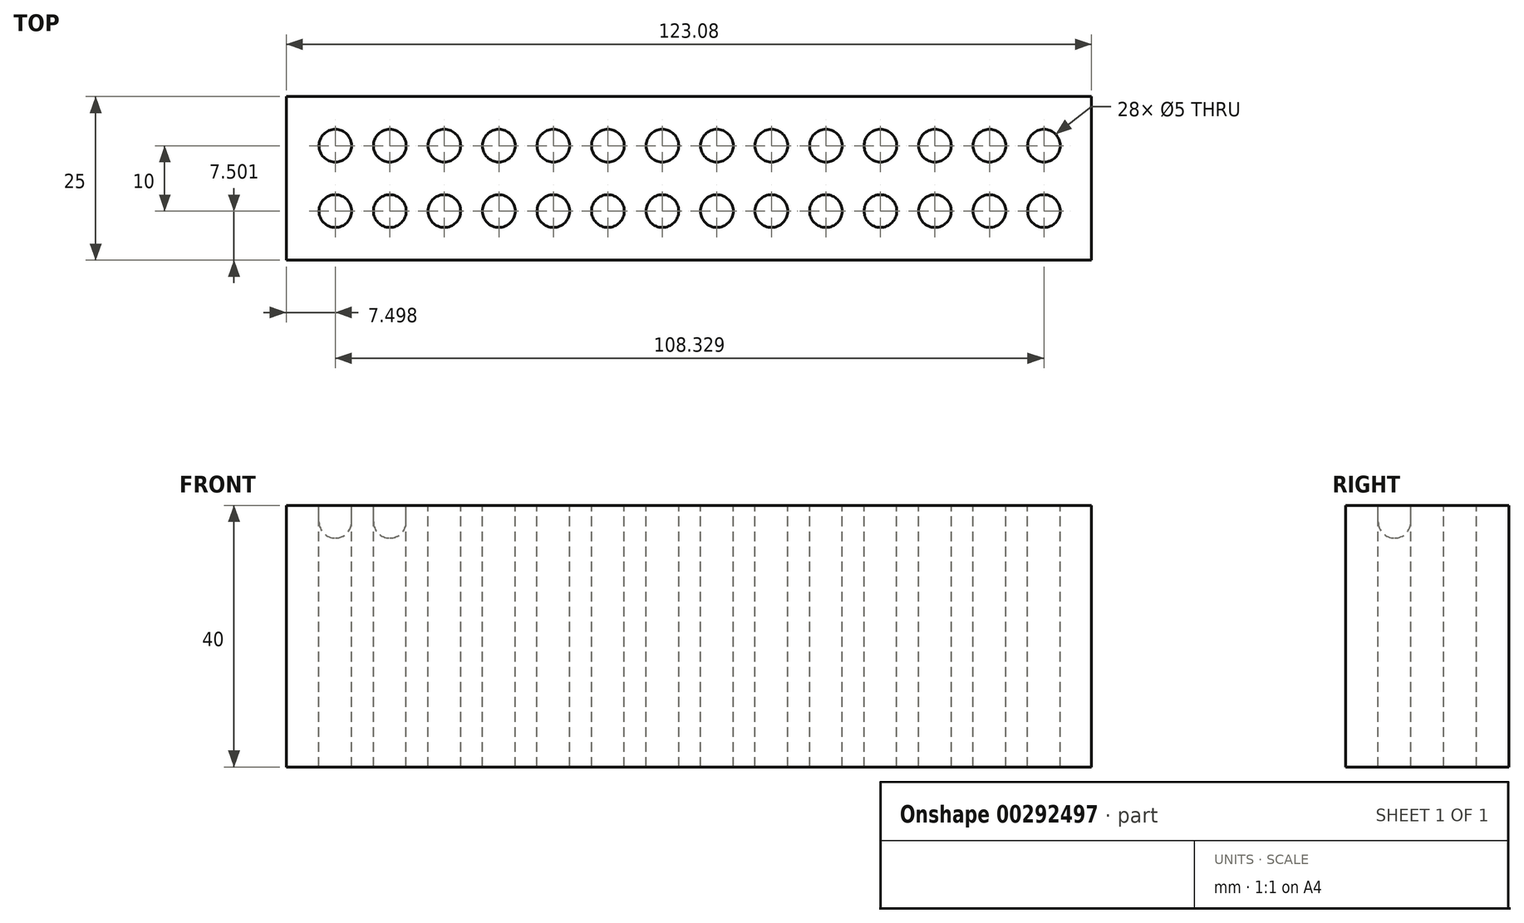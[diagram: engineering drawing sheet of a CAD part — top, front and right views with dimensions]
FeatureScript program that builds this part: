
annotation { "Feature Type Name" : "Feature", "Feature Type Description" : "" }
export const myFeature = defineFeature(function(context is Context, id is Id, definition is map)
    precondition{}
    {
        {
            var Q0;
            Q0=qCreatedBy(makeId("Top.planeOp"),FACE);
            var sketch = newSketch(context, id + "F0", { "sketchPlane" : qUnion([Q0])});
            skLineSegment(sketch, "E0.bottom", {"start": v(-42.9, 15.92) * mm, "end": v(80.2, 15.92) * mm});
            skLineSegment(sketch, "E0.top", {"start": v(-42.9, -9.08) * mm, "end": v(80.2, -9.08) * mm});
            skLineSegment(sketch, "E0.left", {"start": v(-42.9, 15.92) * mm, "end": v(-42.9, -9.08) * mm});
            skLineSegment(sketch, "E0.right", {"start": v(80.2, 15.92) * mm, "end": v(80.2, -9.08) * mm});
            skCircle(sketch, "E1", {"center": v(-35.4, 8.42) * mm, "radius": 2.5 * mm});
            skCircle(sketch, "E2.1.0.0", {"center": v(-27.06, 8.42) * mm, "radius": 2.5 * mm});
            skLineSegment(sketch, "E2.direction1", {"start": v(-35.4, 8.42) * mm, "end": v(-27.06, 8.42) * mm, "construction": true});
            skCircle(sketch, "E3", {"center": v(-35.4, -1.58) * mm, "radius": 2.5 * mm});
            skCircle(sketch, "E4.1.0.0", {"center": v(-27.06, -1.58) * mm, "radius": 2.5 * mm});
            skLineSegment(sketch, "E4.direction1", {"start": v(-35.4, -1.58) * mm, "end": v(-27.06, -1.58) * mm, "construction": true});
            skCircle(sketch, "E5.0.2.0", {"center": v(-18.73, 8.42) * mm, "radius": 2.5 * mm});
            skCircle(sketch, "E5.0.3.0", {"center": v(-10.4, 8.42) * mm, "radius": 2.5 * mm});
            skCircle(sketch, "E5.0.4.0", {"center": v(-2.06, 8.42) * mm, "radius": 2.5 * mm});
            skCircle(sketch, "E5.0.5.0", {"center": v(6.27, 8.42) * mm, "radius": 2.5 * mm});
            skCircle(sketch, "E5.0.6.0", {"center": v(14.6, 8.42) * mm, "radius": 2.5 * mm});
            skCircle(sketch, "E5.0.7.0", {"center": v(22.94, 8.42) * mm, "radius": 2.5 * mm});
            skCircle(sketch, "E5.0.8.0", {"center": v(31.27, 8.42) * mm, "radius": 2.5 * mm});
            skCircle(sketch, "E5.0.9.0", {"center": v(39.6, 8.42) * mm, "radius": 2.5 * mm});
            skCircle(sketch, "E5.0.10.0", {"center": v(47.94, 8.42) * mm, "radius": 2.5 * mm});
            skCircle(sketch, "E5.0.11.0", {"center": v(56.27, 8.42) * mm, "radius": 2.5 * mm});
            skCircle(sketch, "E5.0.12.0", {"center": v(64.6, 8.42) * mm, "radius": 2.5 * mm});
            skCircle(sketch, "E5.0.13.0", {"center": v(72.94, 8.42) * mm, "radius": 2.5 * mm});
            skCircle(sketch, "E6.0.2.0", {"center": v(-18.73, -1.58) * mm, "radius": 2.5 * mm});
            skCircle(sketch, "E6.0.3.0", {"center": v(-10.4, -1.58) * mm, "radius": 2.5 * mm});
            skCircle(sketch, "E6.0.4.0", {"center": v(-2.06, -1.58) * mm, "radius": 2.5 * mm});
            skCircle(sketch, "E6.0.5.0", {"center": v(6.27, -1.58) * mm, "radius": 2.5 * mm});
            skCircle(sketch, "E6.0.6.0", {"center": v(14.6, -1.58) * mm, "radius": 2.5 * mm});
            skCircle(sketch, "E6.0.7.0", {"center": v(22.94, -1.58) * mm, "radius": 2.5 * mm});
            skCircle(sketch, "E6.0.8.0", {"center": v(31.27, -1.58) * mm, "radius": 2.5 * mm});
            skCircle(sketch, "E6.0.9.0", {"center": v(39.6, -1.58) * mm, "radius": 2.5 * mm});
            skCircle(sketch, "E6.0.10.0", {"center": v(47.94, -1.58) * mm, "radius": 2.5 * mm});
            skCircle(sketch, "E6.0.11.0", {"center": v(56.27, -1.58) * mm, "radius": 2.5 * mm});
            skCircle(sketch, "E6.0.12.0", {"center": v(64.6, -1.58) * mm, "radius": 2.5 * mm});
            skCircle(sketch, "E6.0.13.0", {"center": v(72.94, -1.58) * mm, "radius": 2.5 * mm});
            skSolve(sketch);
        }
        {
            var Q0;
            Q0=makeQuery(id+"F0.imprint","IMPRINT",FACE,{"disambiguationData":[TD([[makeQuery(id+"F0.imprint","IMPRINT",EDGE,{"derivedFrom":sQuery(id+"F0.wireOp",EDGE,"E0.bottom")}),-1.0]])]});
            var Q1;
            Q1=makeQuery(id+"F0.imprint","IMPRINT",FACE,{"disambiguationData":[TD([[makeQuery(id+"F0.imprint","IMPRINT",EDGE,{"derivedFrom":sQuery(id+"F0.wireOp",EDGE,"E1")}),1.0]])]});
            var Q2;
            Q2=makeQuery(id+"F0.imprint","IMPRINT",FACE,{"disambiguationData":[TD([[makeQuery(id+"F0.imprint","IMPRINT",EDGE,{"derivedFrom":sQuery(id+"F0.wireOp",EDGE,"E2.1.0.0")}),1.0]])]});
            var Q3;
            Q3=makeQuery(id+"F0.imprint","IMPRINT",FACE,{"disambiguationData":[TD([[makeQuery(id+"F0.imprint","IMPRINT",EDGE,{"derivedFrom":sQuery(id+"F0.wireOp",EDGE,"E2.2.0.0")}),1.0]])]});
            var Q4;
            Q4=makeQuery(id+"F0.imprint","IMPRINT",FACE,{"disambiguationData":[TD([[makeQuery(id+"F0.imprint","IMPRINT",EDGE,{"derivedFrom":sQuery(id+"F0.wireOp",EDGE,"E2.3.0.0")}),1.0]])]});
            var Q5;
            Q5=makeQuery(id+"F0.imprint","IMPRINT",FACE,{"disambiguationData":[TD([[makeQuery(id+"F0.imprint","IMPRINT",EDGE,{"derivedFrom":sQuery(id+"F0.wireOp",EDGE,"E2.4.0.0")}),1.0]])]});
            var Q6;
            Q6=makeQuery(id+"F0.imprint","IMPRINT",FACE,{"disambiguationData":[TD([[makeQuery(id+"F0.imprint","IMPRINT",EDGE,{"derivedFrom":sQuery(id+"F0.wireOp",EDGE,"E2.5.0.0")}),1.0]])]});
            var Q7;
            Q7=makeQuery(id+"F0.imprint","IMPRINT",FACE,{"disambiguationData":[TD([[makeQuery(id+"F0.imprint","IMPRINT",EDGE,{"derivedFrom":sQuery(id+"F0.wireOp",EDGE,"E2.6.0.0")}),1.0]])]});
            var Q8;
            Q8=makeQuery(id+"F0.imprint","IMPRINT",FACE,{"disambiguationData":[TD([[makeQuery(id+"F0.imprint","IMPRINT",EDGE,{"derivedFrom":sQuery(id+"F0.wireOp",EDGE,"E2.7.0.0")}),1.0]])]});
            var Q9;
            Q9=makeQuery(id+"F0.imprint","IMPRINT",FACE,{"disambiguationData":[TD([[makeQuery(id+"F0.imprint","IMPRINT",EDGE,{"derivedFrom":sQuery(id+"F0.wireOp",EDGE,"E2.8.0.0")}),1.0]])]});
            var Q10;
            Q10=makeQuery(id+"F0.imprint","IMPRINT",FACE,{"disambiguationData":[TD([[makeQuery(id+"F0.imprint","IMPRINT",EDGE,{"derivedFrom":sQuery(id+"F0.wireOp",EDGE,"E2.9.0.0")}),1.0]])]});
            var Q11;
            Q11=makeQuery(id+"F0.imprint","IMPRINT",FACE,{"disambiguationData":[TD([[makeQuery(id+"F0.imprint","IMPRINT",EDGE,{"derivedFrom":sQuery(id+"F0.wireOp",EDGE,"E2.10.0.0")}),1.0]])]});
            var Q12;
            Q12=makeQuery(id+"F0.imprint","IMPRINT",FACE,{"disambiguationData":[TD([[makeQuery(id+"F0.imprint","IMPRINT",EDGE,{"derivedFrom":sQuery(id+"F0.wireOp",EDGE,"E2.11.0.0")}),1.0]])]});
            var Q13;
            Q13=makeQuery(id+"F0.imprint","IMPRINT",FACE,{"disambiguationData":[TD([[makeQuery(id+"F0.imprint","IMPRINT",EDGE,{"derivedFrom":sQuery(id+"F0.wireOp",EDGE,"E2.12.0.0")}),1.0]])]});
            var Q14;
            Q14=makeQuery(id+"F0.imprint","IMPRINT",FACE,{"disambiguationData":[TD([[makeQuery(id+"F0.imprint","IMPRINT",EDGE,{"derivedFrom":sQuery(id+"F0.wireOp",EDGE,"E2.13.0.0")}),1.0]])]});
            var Q15;
            Q15=makeQuery(id+"F0.imprint","IMPRINT",FACE,{"disambiguationData":[TD([[makeQuery(id+"F0.imprint","IMPRINT",EDGE,{"derivedFrom":sQuery(id+"F0.wireOp",EDGE,"E2.14.0.0")}),1.0]])]});
            var Q16;
            Q16=makeQuery(id+"F0.imprint","IMPRINT",FACE,{"disambiguationData":[TD([[makeQuery(id+"F0.imprint","IMPRINT",EDGE,{"derivedFrom":sQuery(id+"F0.wireOp",EDGE,"E4.14.0.0")}),1.0]])]});
            var Q17;
            Q17=makeQuery(id+"F0.imprint","IMPRINT",FACE,{"disambiguationData":[TD([[makeQuery(id+"F0.imprint","IMPRINT",EDGE,{"derivedFrom":sQuery(id+"F0.wireOp",EDGE,"E4.13.0.0")}),1.0]])]});
            var Q18;
            Q18=makeQuery(id+"F0.imprint","IMPRINT",FACE,{"disambiguationData":[TD([[makeQuery(id+"F0.imprint","IMPRINT",EDGE,{"derivedFrom":sQuery(id+"F0.wireOp",EDGE,"E4.12.0.0")}),1.0]])]});
            var Q19;
            Q19=makeQuery(id+"F0.imprint","IMPRINT",FACE,{"disambiguationData":[TD([[makeQuery(id+"F0.imprint","IMPRINT",EDGE,{"derivedFrom":sQuery(id+"F0.wireOp",EDGE,"E4.11.0.0")}),1.0]])]});
            var Q20;
            Q20=makeQuery(id+"F0.imprint","IMPRINT",FACE,{"disambiguationData":[TD([[makeQuery(id+"F0.imprint","IMPRINT",EDGE,{"derivedFrom":sQuery(id+"F0.wireOp",EDGE,"E4.10.0.0")}),1.0]])]});
            var Q21;
            Q21=makeQuery(id+"F0.imprint","IMPRINT",FACE,{"disambiguationData":[TD([[makeQuery(id+"F0.imprint","IMPRINT",EDGE,{"derivedFrom":sQuery(id+"F0.wireOp",EDGE,"E4.9.0.0")}),1.0]])]});
            var Q22;
            Q22=makeQuery(id+"F0.imprint","IMPRINT",FACE,{"disambiguationData":[TD([[makeQuery(id+"F0.imprint","IMPRINT",EDGE,{"derivedFrom":sQuery(id+"F0.wireOp",EDGE,"E4.8.0.0")}),1.0]])]});
            var Q23;
            Q23=makeQuery(id+"F0.imprint","IMPRINT",FACE,{"disambiguationData":[TD([[makeQuery(id+"F0.imprint","IMPRINT",EDGE,{"derivedFrom":sQuery(id+"F0.wireOp",EDGE,"E4.7.0.0")}),1.0]])]});
            var Q24;
            Q24=makeQuery(id+"F0.imprint","IMPRINT",FACE,{"disambiguationData":[TD([[makeQuery(id+"F0.imprint","IMPRINT",EDGE,{"derivedFrom":sQuery(id+"F0.wireOp",EDGE,"E4.6.0.0")}),1.0]])]});
            var Q25;
            Q25=makeQuery(id+"F0.imprint","IMPRINT",FACE,{"disambiguationData":[TD([[makeQuery(id+"F0.imprint","IMPRINT",EDGE,{"derivedFrom":sQuery(id+"F0.wireOp",EDGE,"E4.5.0.0")}),1.0]])]});
            var Q26;
            Q26=makeQuery(id+"F0.imprint","IMPRINT",FACE,{"disambiguationData":[TD([[makeQuery(id+"F0.imprint","IMPRINT",EDGE,{"derivedFrom":sQuery(id+"F0.wireOp",EDGE,"E4.4.0.0")}),1.0]])]});
            var Q27;
            Q27=makeQuery(id+"F0.imprint","IMPRINT",FACE,{"disambiguationData":[TD([[makeQuery(id+"F0.imprint","IMPRINT",EDGE,{"derivedFrom":sQuery(id+"F0.wireOp",EDGE,"E4.3.0.0")}),1.0]])]});
            var Q28;
            Q28=makeQuery(id+"F0.imprint","IMPRINT",FACE,{"disambiguationData":[TD([[makeQuery(id+"F0.imprint","IMPRINT",EDGE,{"derivedFrom":sQuery(id+"F0.wireOp",EDGE,"E4.2.0.0")}),1.0]])]});
            var Q29;
            Q29=makeQuery(id+"F0.imprint","IMPRINT",FACE,{"disambiguationData":[TD([[makeQuery(id+"F0.imprint","IMPRINT",EDGE,{"derivedFrom":sQuery(id+"F0.wireOp",EDGE,"E4.1.0.0")}),1.0]])]});
            var Q30;
            Q30=makeQuery(id+"F0.imprint","IMPRINT",FACE,{"disambiguationData":[TD([[makeQuery(id+"F0.imprint","IMPRINT",EDGE,{"derivedFrom":sQuery(id+"F0.wireOp",EDGE,"E3")}),1.0]])]});
            extrude(context, id + "F1", {"entities" : qUnion([Q0, Q1, Q2, Q3, Q4, Q5, Q6, Q7, Q8, Q9, Q10, Q11, Q12, Q13, Q14, Q15, Q16, Q17, Q18, Q19, Q20, Q21, Q22, Q23, Q24, Q25, Q26, Q27, Q28, Q29, Q30]), "oppositeDirection" : true, "depth" : 40 * mm});
        }
        {
            var Q0;
            Q0=makeQuery(id+"F0.imprint","IMPRINT",FACE,{"disambiguationData":[TD([[makeQuery(id+"F0.imprint","IMPRINT",EDGE,{"derivedFrom":sQuery(id+"F0.wireOp",EDGE,"E1")}),1.0]])]});
            var Q1;
            Q1=makeQuery(id+"F0.imprint","IMPRINT",FACE,{"disambiguationData":[TD([[makeQuery(id+"F0.imprint","IMPRINT",EDGE,{"derivedFrom":sQuery(id+"F0.wireOp",EDGE,"E2.1.0.0")}),1.0]])]});
            var Q2;
            Q2=makeQuery(id+"F0.imprint","IMPRINT",FACE,{"disambiguationData":[TD([[makeQuery(id+"F0.imprint","IMPRINT",EDGE,{"derivedFrom":sQuery(id+"F0.wireOp",EDGE,"E5.0.2.0")}),1.0]])]});
            var Q3;
            Q3=makeQuery(id+"F0.imprint","IMPRINT",FACE,{"disambiguationData":[TD([[makeQuery(id+"F0.imprint","IMPRINT",EDGE,{"derivedFrom":sQuery(id+"F0.wireOp",EDGE,"E5.0.3.0")}),1.0]])]});
            var Q4;
            Q4=makeQuery(id+"F0.imprint","IMPRINT",FACE,{"disambiguationData":[TD([[makeQuery(id+"F0.imprint","IMPRINT",EDGE,{"derivedFrom":sQuery(id+"F0.wireOp",EDGE,"E5.0.4.0")}),1.0]])]});
            var Q5;
            Q5=makeQuery(id+"F0.imprint","IMPRINT",FACE,{"disambiguationData":[TD([[makeQuery(id+"F0.imprint","IMPRINT",EDGE,{"derivedFrom":sQuery(id+"F0.wireOp",EDGE,"E5.0.5.0")}),1.0]])]});
            var Q6;
            Q6=makeQuery(id+"F0.imprint","IMPRINT",FACE,{"disambiguationData":[TD([[makeQuery(id+"F0.imprint","IMPRINT",EDGE,{"derivedFrom":sQuery(id+"F0.wireOp",EDGE,"E5.0.6.0")}),1.0]])]});
            var Q7;
            Q7=makeQuery(id+"F0.imprint","IMPRINT",FACE,{"disambiguationData":[TD([[makeQuery(id+"F0.imprint","IMPRINT",EDGE,{"derivedFrom":sQuery(id+"F0.wireOp",EDGE,"E5.0.7.0")}),1.0]])]});
            var Q8;
            Q8=makeQuery(id+"F0.imprint","IMPRINT",FACE,{"disambiguationData":[TD([[makeQuery(id+"F0.imprint","IMPRINT",EDGE,{"derivedFrom":sQuery(id+"F0.wireOp",EDGE,"E5.0.8.0")}),1.0]])]});
            var Q9;
            Q9=makeQuery(id+"F0.imprint","IMPRINT",FACE,{"disambiguationData":[TD([[makeQuery(id+"F0.imprint","IMPRINT",EDGE,{"derivedFrom":sQuery(id+"F0.wireOp",EDGE,"E5.0.9.0")}),1.0]])]});
            var Q10;
            Q10=makeQuery(id+"F0.imprint","IMPRINT",FACE,{"disambiguationData":[TD([[makeQuery(id+"F0.imprint","IMPRINT",EDGE,{"derivedFrom":sQuery(id+"F0.wireOp",EDGE,"E5.0.10.0")}),1.0]])]});
            var Q11;
            Q11=makeQuery(id+"F0.imprint","IMPRINT",FACE,{"disambiguationData":[TD([[makeQuery(id+"F0.imprint","IMPRINT",EDGE,{"derivedFrom":sQuery(id+"F0.wireOp",EDGE,"E5.0.11.0")}),1.0]])]});
            var Q12;
            Q12=makeQuery(id+"F0.imprint","IMPRINT",FACE,{"disambiguationData":[TD([[makeQuery(id+"F0.imprint","IMPRINT",EDGE,{"derivedFrom":sQuery(id+"F0.wireOp",EDGE,"E5.0.12.0")}),1.0]])]});
            var Q13;
            Q13=makeQuery(id+"F0.imprint","IMPRINT",FACE,{"disambiguationData":[TD([[makeQuery(id+"F0.imprint","IMPRINT",EDGE,{"derivedFrom":sQuery(id+"F0.wireOp",EDGE,"E5.0.13.0")}),1.0]])]});
            extrude(context, id + "F2", {"entities" : qUnion([Q0, Q1, Q2, Q3, Q4, Q5, Q6, Q7, Q8, Q9, Q10, Q11, Q12, Q13]), "operationType" : NewBodyOperationType.REMOVE, "oppositeDirection" : true, "depth" : 40 * mm});
        }
        {
            var Q0;
            Q0=makeQuery(id+"F0.imprint","IMPRINT",FACE,{"disambiguationData":[TD([[makeQuery(id+"F0.imprint","IMPRINT",EDGE,{"derivedFrom":sQuery(id+"F0.wireOp",EDGE,"E3")}),1.0]])]});
            var Q1;
            Q1=makeQuery(id+"F0.imprint","IMPRINT",FACE,{"disambiguationData":[TD([[makeQuery(id+"F0.imprint","IMPRINT",EDGE,{"derivedFrom":sQuery(id+"F0.wireOp",EDGE,"E4.1.0.0")}),1.0]])]});
            var Q2;
            Q2=makeQuery(id+"F0.imprint","IMPRINT",FACE,{"disambiguationData":[TD([[makeQuery(id+"F0.imprint","IMPRINT",EDGE,{"derivedFrom":sQuery(id+"F0.wireOp",EDGE,"E4.2.0.0")}),1.0]])]});
            var Q3;
            Q3=makeQuery(id+"F0.imprint","IMPRINT",FACE,{"disambiguationData":[TD([[makeQuery(id+"F0.imprint","IMPRINT",EDGE,{"derivedFrom":sQuery(id+"F0.wireOp",EDGE,"E4.3.0.0")}),1.0]])]});
            var Q4;
            Q4=makeQuery(id+"F0.imprint","IMPRINT",FACE,{"disambiguationData":[TD([[makeQuery(id+"F0.imprint","IMPRINT",EDGE,{"derivedFrom":sQuery(id+"F0.wireOp",EDGE,"E4.4.0.0")}),1.0]])]});
            var Q5;
            Q5=makeQuery(id+"F0.imprint","IMPRINT",FACE,{"disambiguationData":[TD([[makeQuery(id+"F0.imprint","IMPRINT",EDGE,{"derivedFrom":sQuery(id+"F0.wireOp",EDGE,"E4.5.0.0")}),1.0]])]});
            var Q6;
            Q6=makeQuery(id+"F0.imprint","IMPRINT",FACE,{"disambiguationData":[TD([[makeQuery(id+"F0.imprint","IMPRINT",EDGE,{"derivedFrom":sQuery(id+"F0.wireOp",EDGE,"E4.6.0.0")}),1.0]])]});
            var Q7;
            Q7=makeQuery(id+"F0.imprint","IMPRINT",FACE,{"disambiguationData":[TD([[makeQuery(id+"F0.imprint","IMPRINT",EDGE,{"derivedFrom":sQuery(id+"F0.wireOp",EDGE,"E4.7.0.0")}),1.0]])]});
            var Q8;
            Q8=makeQuery(id+"F0.imprint","IMPRINT",FACE,{"disambiguationData":[TD([[makeQuery(id+"F0.imprint","IMPRINT",EDGE,{"derivedFrom":sQuery(id+"F0.wireOp",EDGE,"E4.8.0.0")}),1.0]])]});
            var Q9;
            Q9=makeQuery(id+"F0.imprint","IMPRINT",FACE,{"disambiguationData":[TD([[makeQuery(id+"F0.imprint","IMPRINT",EDGE,{"derivedFrom":sQuery(id+"F0.wireOp",EDGE,"E4.9.0.0")}),1.0]])]});
            var Q10;
            Q10=makeQuery(id+"F0.imprint","IMPRINT",FACE,{"disambiguationData":[TD([[makeQuery(id+"F0.imprint","IMPRINT",EDGE,{"derivedFrom":sQuery(id+"F0.wireOp",EDGE,"E4.10.0.0")}),1.0]])]});
            var Q11;
            Q11=makeQuery(id+"F0.imprint","IMPRINT",FACE,{"disambiguationData":[TD([[makeQuery(id+"F0.imprint","IMPRINT",EDGE,{"derivedFrom":sQuery(id+"F0.wireOp",EDGE,"E4.11.0.0")}),1.0]])]});
            var Q12;
            Q12=makeQuery(id+"F0.imprint","IMPRINT",FACE,{"disambiguationData":[TD([[makeQuery(id+"F0.imprint","IMPRINT",EDGE,{"derivedFrom":sQuery(id+"F0.wireOp",EDGE,"E4.12.0.0")}),1.0]])]});
            var Q13;
            Q13=makeQuery(id+"F0.imprint","IMPRINT",FACE,{"disambiguationData":[TD([[makeQuery(id+"F0.imprint","IMPRINT",EDGE,{"derivedFrom":sQuery(id+"F0.wireOp",EDGE,"E4.13.0.0")}),1.0]])]});
            var Q14;
            Q14=makeQuery(id+"F0.imprint","IMPRINT",FACE,{"disambiguationData":[TD([[makeQuery(id+"F0.imprint","IMPRINT",EDGE,{"derivedFrom":sQuery(id+"F0.wireOp",EDGE,"E4.14.0.0")}),1.0]])]});
            extrude(context, id + "F3", {"entities" : qUnion([Q0, Q1, Q2, Q3, Q4, Q5, Q6, Q7, Q8, Q9, Q10, Q11, Q12, Q13, Q14]), "operationType" : NewBodyOperationType.REMOVE, "oppositeDirection" : true, "depth" : 5 * mm});
        }
        {
            var Q0;
            Q0=makeQuery(id+"F3.boolean.opBoolean","COPY",EDGE,{"derivedFrom":makeQuery(id+"F3.opExtrude","CAP_EDGE",EDGE,{"disambiguationData":[OSD([sQuery(id+"F0.wireOp",EDGE,"E3")])],"isStart":false})});
            var Q1;
            Q1=makeQuery(id+"F3.boolean.opBoolean","COPY",EDGE,{"derivedFrom":makeQuery(id+"F3.opExtrude","CAP_EDGE",EDGE,{"disambiguationData":[OSD([sQuery(id+"F0.wireOp",EDGE,"E4.1.0.0")])],"isStart":false})});
            var Q2;
            Q2=makeQuery(id+"F3.boolean.opBoolean","COPY",EDGE,{"derivedFrom":makeQuery(id+"F3.opExtrude","CAP_EDGE",EDGE,{"disambiguationData":[OSD([sQuery(id+"F0.wireOp",EDGE,"E4.2.0.0")])],"isStart":false})});
            var Q3;
            Q3=makeQuery(id+"F3.boolean.opBoolean","COPY",EDGE,{"derivedFrom":makeQuery(id+"F3.opExtrude","CAP_EDGE",EDGE,{"disambiguationData":[OSD([sQuery(id+"F0.wireOp",EDGE,"E4.3.0.0")])],"isStart":false})});
            var Q4;
            Q4=makeQuery(id+"F3.boolean.opBoolean","COPY",EDGE,{"derivedFrom":makeQuery(id+"F3.opExtrude","CAP_EDGE",EDGE,{"disambiguationData":[OSD([sQuery(id+"F0.wireOp",EDGE,"E4.4.0.0")])],"isStart":false})});
            var Q5;
            Q5=makeQuery(id+"F3.boolean.opBoolean","COPY",EDGE,{"derivedFrom":makeQuery(id+"F3.opExtrude","CAP_EDGE",EDGE,{"disambiguationData":[OSD([sQuery(id+"F0.wireOp",EDGE,"E4.5.0.0")])],"isStart":false})});
            var Q6;
            Q6=makeQuery(id+"F3.boolean.opBoolean","COPY",EDGE,{"derivedFrom":makeQuery(id+"F3.opExtrude","CAP_EDGE",EDGE,{"disambiguationData":[OSD([sQuery(id+"F0.wireOp",EDGE,"E4.6.0.0")])],"isStart":false})});
            var Q7;
            Q7=makeQuery(id+"F3.boolean.opBoolean","COPY",EDGE,{"derivedFrom":makeQuery(id+"F3.opExtrude","CAP_EDGE",EDGE,{"disambiguationData":[OSD([sQuery(id+"F0.wireOp",EDGE,"E4.7.0.0")])],"isStart":false})});
            var Q8;
            Q8=makeQuery(id+"F3.boolean.opBoolean","COPY",FACE,{"derivedFrom":makeQuery(id+"F3.opExtrude","CAP_FACE",FACE,{"disambiguationData":[OSD([sQuery(id+"F0.wireOp",EDGE,"E4.8.0.0")])],"isStart":false})});
            var Q9;
            Q9=makeQuery(id+"F3.boolean.opBoolean","COPY",EDGE,{"derivedFrom":makeQuery(id+"F3.opExtrude","CAP_EDGE",EDGE,{"disambiguationData":[OSD([sQuery(id+"F0.wireOp",EDGE,"E4.9.0.0")])],"isStart":false})});
            var Q10;
            Q10=makeQuery(id+"F3.boolean.opBoolean","COPY",EDGE,{"derivedFrom":makeQuery(id+"F3.opExtrude","CAP_EDGE",EDGE,{"disambiguationData":[OSD([sQuery(id+"F0.wireOp",EDGE,"E4.10.0.0")])],"isStart":false})});
            var Q11;
            Q11=makeQuery(id+"F3.boolean.opBoolean","COPY",FACE,{"derivedFrom":makeQuery(id+"F3.opExtrude","CAP_FACE",FACE,{"disambiguationData":[OSD([sQuery(id+"F0.wireOp",EDGE,"E4.11.0.0")])],"isStart":false})});
            var Q12;
            Q12=makeQuery(id+"F3.boolean.opBoolean","COPY",FACE,{"derivedFrom":makeQuery(id+"F3.opExtrude","CAP_FACE",FACE,{"disambiguationData":[OSD([sQuery(id+"F0.wireOp",EDGE,"E4.12.0.0")])],"isStart":false})});
            var Q13;
            Q13=makeQuery(id+"F3.boolean.opBoolean","COPY",EDGE,{"derivedFrom":makeQuery(id+"F3.opExtrude","CAP_EDGE",EDGE,{"disambiguationData":[OSD([sQuery(id+"F0.wireOp",EDGE,"E4.13.0.0")])],"isStart":false})});
            var Q14;
            Q14=makeQuery(id+"F3.boolean.opBoolean","COPY",EDGE,{"derivedFrom":makeQuery(id+"F3.opExtrude","CAP_EDGE",EDGE,{"disambiguationData":[OSD([sQuery(id+"F0.wireOp",EDGE,"E4.14.0.0")])],"isStart":false})});
            fillet(context, id + "F4", {"entities" : qUnion([Q0, Q1, Q2, Q3, Q4, Q5, Q6, Q7, Q8, Q9, Q10, Q11, Q12, Q13, Q14]), "radius" : 2.5 * mm, "tangentPropagation" : true, "allowEdgeOverflow" : false});
        }
    });
